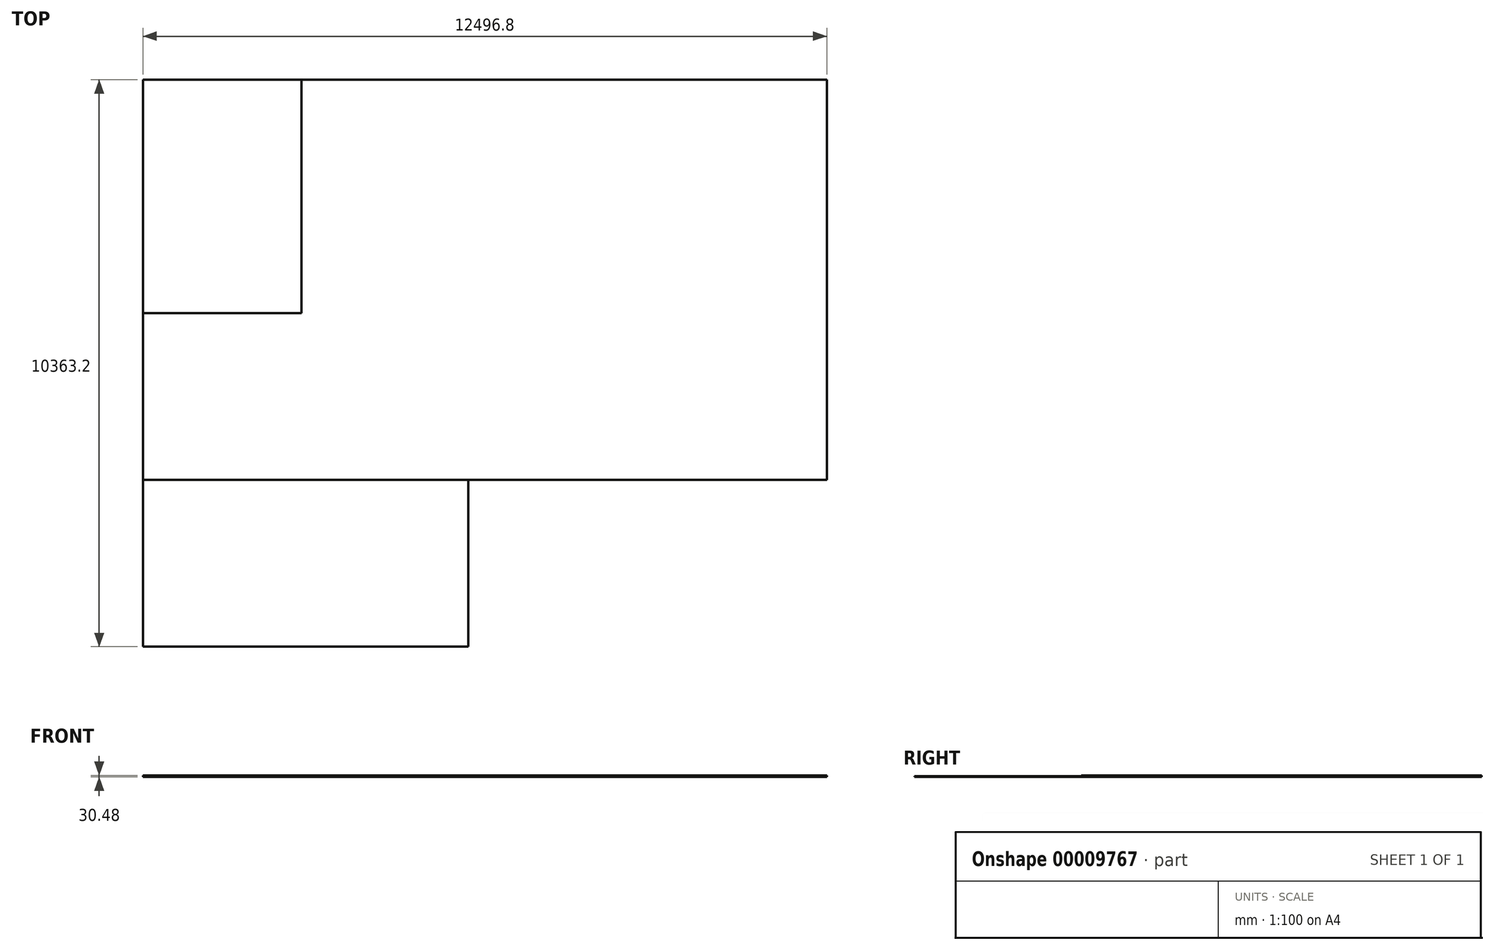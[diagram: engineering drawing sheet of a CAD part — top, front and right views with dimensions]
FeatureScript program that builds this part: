
annotation { "Feature Type Name" : "Feature", "Feature Type Description" : "" }
export const myFeature = defineFeature(function(context is Context, id is Id, definition is map)
    precondition{}
    {
        {
            var Q0;
            Q0=qCreatedBy(makeId("Top.planeOp"),FACE);
            var sketch = newSketch(context, id + "F0", { "sketchPlane" : qUnion([Q0])});
            skLineSegment(sketch, "E0.bottom", {"start": v(-4800.6, 3657.6) * mm, "end": v(4800.6, 3657.6) * mm});
            skLineSegment(sketch, "E0.top", {"start": v(-4800.6, -3657.6) * mm, "end": v(4800.6, -3657.6) * mm});
            skLineSegment(sketch, "E0.left", {"start": v(-4800.6, 3657.6) * mm, "end": v(-4800.6, -3657.6) * mm});
            skLineSegment(sketch, "E0.right", {"start": v(4800.6, 3657.6) * mm, "end": v(4800.6, -3657.6) * mm});
            skLineSegment(sketch, "E1.bottom", {"start": v(-4800.6, -3657.6) * mm, "end": v(-7696.2, -3657.6) * mm});
            skLineSegment(sketch, "E1.top", {"start": v(-4800.6, -609.6) * mm, "end": v(-7696.2, -609.6) * mm});
            skLineSegment(sketch, "E1.left", {"start": v(-4800.6, -3657.6) * mm, "end": v(-4800.6, -609.6) * mm});
            skLineSegment(sketch, "E1.right", {"start": v(-7696.2, -3657.6) * mm, "end": v(-7696.2, -609.6) * mm});
            skSolve(sketch);
        }
        {
            var Q0;
            Q0=qCreatedBy(makeId("Top.planeOp"),FACE);
            var sketch = newSketch(context, id + "F1", { "sketchPlane" : qUnion([Q0])});
            skLineSegment(sketch, "E2", {"start": v(-7696.2, 3657.6) * mm, "end": v(-7696.2, -6705.6) * mm});
            skLineSegment(sketch, "E3", {"start": v(-7696.2, -6705.6) * mm, "end": v(-1752.6, -6705.6) * mm});
            skLineSegment(sketch, "E4", {"start": v(-1752.6, -6705.6) * mm, "end": v(-1752.6, -3657.6) * mm});
            skLineSegment(sketch, "E5.0", {"start": v(-7696.2, 3657.6) * mm, "end": v(-4800.6, 3657.6) * mm});
            skLineSegment(sketch, "E6.0", {"start": v(-4800.6, -3657.6) * mm, "end": v(-1752.6, -3657.6) * mm});
            skLineSegment(sketch, "E7.0", {"start": v(-4800.6, 3657.6) * mm, "end": v(-4800.6, -3657.6) * mm});
            skPoint(sketch, "E8.orphan", {"position": v(4800.6, -3657.6) * mm});
            skPoint(sketch, "E9.orphan", {"position": v(4800.6, 3657.6) * mm});
            skPoint(sketch, "E10.orphan", {"position": v(-4800.6, 3657.6) * mm});
            skSolve(sketch);
        }
        {
            var Q0;
            Q0=makeQuery(id+"F0.imprint","IMPRINT",FACE,{"disambiguationData":[TD([[makeQuery(id+"F0.imprint","IMPRINT",EDGE,{"derivedFrom":sQuery(id+"F0.wireOp",EDGE,"E0.bottom")}),-1.0]])]});
            var Q1;
            Q1=makeQuery(id+"F0.imprint","IMPRINT",FACE,{"disambiguationData":[TD([[makeQuery(id+"F0.imprint","IMPRINT",EDGE,{"derivedFrom":sQuery(id+"F0.wireOp",EDGE,"E1.bottom")}),-1.0]])]});
            extrude(context, id + "F2", {"entities" : qUnion([Q0, Q1]), "depth" : 30.48 * mm});
        }
        {
            var Q0;
            Q0 = qSketchRegion(id + "F1", true);
            extrude(context, id + "F3", {"entities" : qUnion([Q0]), "depth" : 15.24 * mm});
        }
    });
